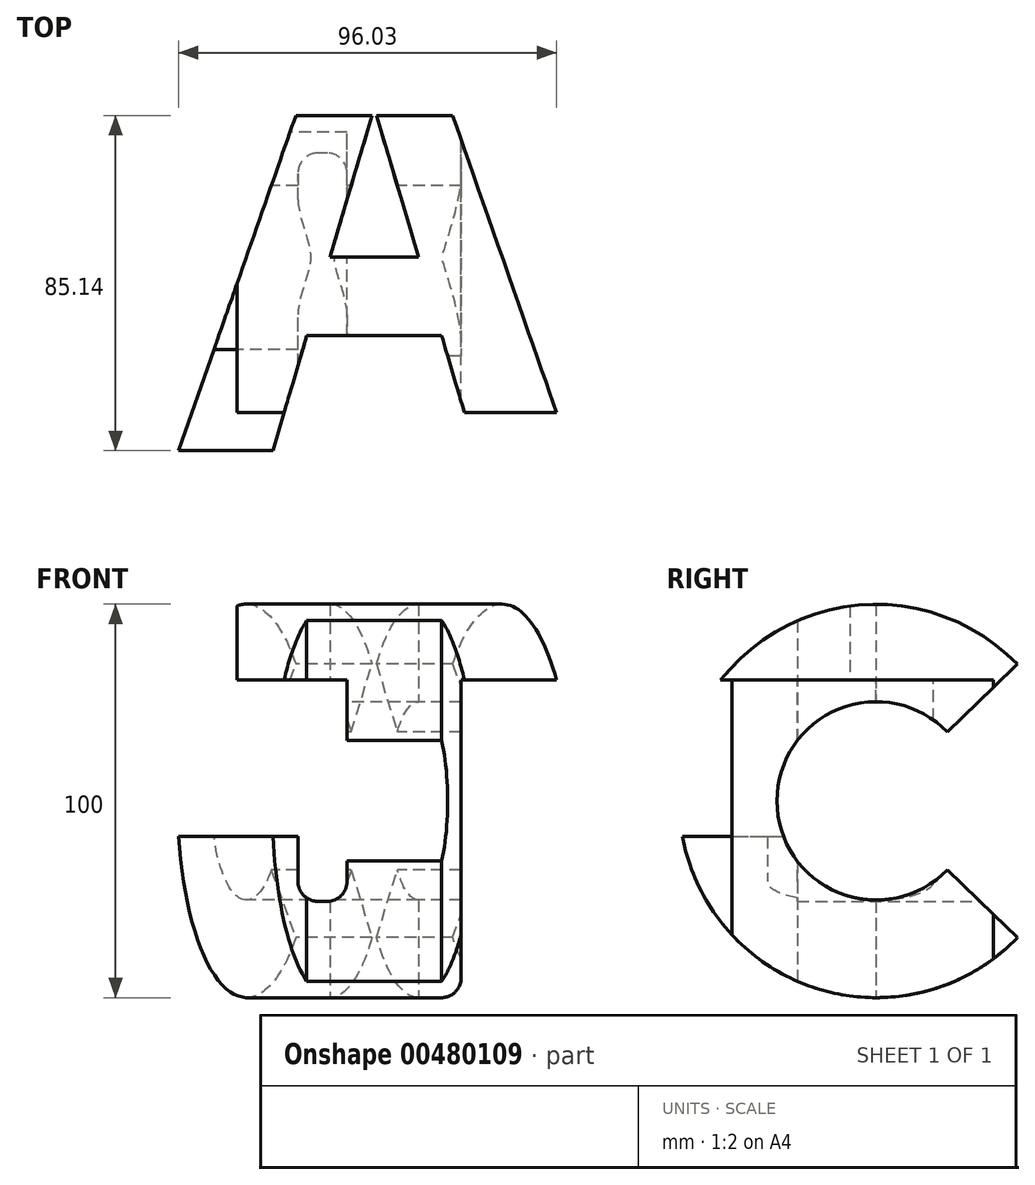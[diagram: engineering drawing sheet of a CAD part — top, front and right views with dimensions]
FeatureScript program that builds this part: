
annotation { "Feature Type Name" : "Feature", "Feature Type Description" : "" }
export const myFeature = defineFeature(function(context is Context, id is Id, definition is map)
    precondition{}
    {
        {
            var Q0;
            Q0=qCreatedBy(makeId("Top.planeOp"),FACE);
            var sketch = newSketch(context, id + "F0", { "sketchPlane" : qUnion([Q0])});
            skLineSegment(sketch, "E0.bottom", {"start": v(50, 50) * mm, "end": v(-50, 50) * mm, "construction": true});
            skLineSegment(sketch, "E0.top", {"start": v(50, -50) * mm, "end": v(-50, -50) * mm, "construction": true});
            skLineSegment(sketch, "E0.left", {"start": v(50, 50) * mm, "end": v(50, -50) * mm, "construction": true});
            skLineSegment(sketch, "E0.right", {"start": v(-50, 50) * mm, "end": v(-50, -50) * mm, "construction": true});
            skPoint(sketch, "E0.middle", {"position": v(0, 0) * mm});
            skLineSegment(sketch, "E1", {"start": v(0, 50) * mm, "end": v(15, 50) * mm});
            skLineSegment(sketch, "E2", {"start": v(0, 50) * mm, "end": v(-15, 50) * mm});
            skLineSegment(sketch, "E3", {"start": v(-50, -50) * mm, "end": v(-15, 50) * mm});
            skLineSegment(sketch, "E4", {"start": v(15, 50) * mm, "end": v(50, -50) * mm});
            skLineSegment(sketch, "E5", {"start": v(-26.01, -50) * mm, "end": v(-17.14, -20) * mm});
            skLineSegment(sketch, "E6", {"start": v(0, 37.9) * mm, "end": v(11.22, 0) * mm});
            skLineSegment(sketch, "E7", {"start": v(-50, -50) * mm, "end": v(-26.01, -50) * mm});
            skLineSegment(sketch, "E8", {"start": v(26.01, -50) * mm, "end": v(50, -50) * mm});
            skLineSegment(sketch, "E9", {"start": v(-11.22, 0) * mm, "end": v(11.22, 0) * mm});
            skLineSegment(sketch, "E10", {"start": v(-17.14, -20) * mm, "end": v(17.14, -20) * mm});
            skLineSegment(sketch, "E11.trimOffspring", {"start": v(-11.22, 0) * mm, "end": v(0, 37.9) * mm});
            skLineSegment(sketch, "E12.trimOffspring", {"start": v(17.14, -20) * mm, "end": v(26.01, -50) * mm});
            skSolve(sketch);
        }
        {
            var Q0;
            Q0=qCreatedBy(makeId("Front.planeOp"),FACE);
            var sketch = newSketch(context, id + "F1", { "sketchPlane" : qUnion([Q0])});
            skLineSegment(sketch, "E13.bottom", {"start": v(50, 50) * mm, "end": v(-50, 50) * mm, "construction": true});
            skLineSegment(sketch, "E13.top", {"start": v(50, -50) * mm, "end": v(-50, -50) * mm, "construction": true});
            skLineSegment(sketch, "E13.left", {"start": v(50, 50) * mm, "end": v(50, -50) * mm, "construction": true});
            skLineSegment(sketch, "E13.right", {"start": v(-50, 50) * mm, "end": v(-50, -50) * mm, "construction": true});
            skPoint(sketch, "E13.middle", {"position": v(0, 0) * mm});
            skLineSegment(sketch, "E14.bottom", {"start": v(50, 50) * mm, "end": v(-34.84, 50) * mm});
            skLineSegment(sketch, "E14.top", {"start": v(50, 30.68) * mm, "end": v(22.07, 30.68) * mm});
            skLineSegment(sketch, "E14.left", {"start": v(50, 50) * mm, "end": v(50, 30.68) * mm});
            skLineSegment(sketch, "E14.right", {"start": v(-34.84, 50) * mm, "end": v(-34.84, 30.68) * mm});
            skLineSegment(sketch, "E15", {"start": v(22.07, 30.68) * mm, "end": v(22.07, -45) * mm});
            skLineSegment(sketch, "E16", {"start": v(17.07, -50) * mm, "end": v(-45, -50) * mm});
            skLineSegment(sketch, "E17", {"start": v(-50, -45) * mm, "end": v(-50, -9.07) * mm});
            skLineSegment(sketch, "E18", {"start": v(-50, -9.07) * mm, "end": v(-19.37, -9.07) * mm});
            skLineSegment(sketch, "E19", {"start": v(-19.37, -9.07) * mm, "end": v(-19.37, -20.52) * mm});
            skLineSegment(sketch, "E20", {"start": v(-14.37, -25.52) * mm, "end": v(-11.9, -25.52) * mm});
            skLineSegment(sketch, "E21", {"start": v(-6.9, -20.52) * mm, "end": v(-6.9, 30.68) * mm});
            skPoint(sketch, "E22.visualSharp", {"position": v(22.07, -50) * mm});
            skArc(sketch, "E22.filletArc", {"start": v(17.07, -50) * mm, "mid": v(20.6, -48.54) * mm, "end": v(22.07, -45) * mm});
            skPoint(sketch, "E23.visualSharp", {"position": v(-50, -50) * mm});
            skArc(sketch, "E23.filletArc", {"start": v(-50, -45) * mm, "mid": v(-48.54, -48.54) * mm, "end": v(-45, -50) * mm});
            skPoint(sketch, "E24.visualSharp", {"position": v(-19.37, -25.52) * mm});
            skArc(sketch, "E24.filletArc", {"start": v(-19.37, -20.52) * mm, "mid": v(-17.9, -24.06) * mm, "end": v(-14.37, -25.52) * mm});
            skPoint(sketch, "E25.visualSharp", {"position": v(-6.9, -25.52) * mm});
            skArc(sketch, "E25.filletArc", {"start": v(-11.9, -25.52) * mm, "mid": v(-8.37, -24.06) * mm, "end": v(-6.9, -20.52) * mm});
            skLineSegment(sketch, "E26.trimOffspring", {"start": v(-6.9, 30.68) * mm, "end": v(-34.84, 30.68) * mm});
            skSolve(sketch);
        }
        {
            var Q0;
            Q0=qCreatedBy(makeId("Right.planeOp"),FACE);
            var sketch = newSketch(context, id + "F2", { "sketchPlane" : qUnion([Q0])});
            skLineSegment(sketch, "E27.bottom", {"start": v(50, 50) * mm, "end": v(-50, 50) * mm, "construction": true});
            skLineSegment(sketch, "E27.top", {"start": v(50, -50) * mm, "end": v(-50, -50) * mm, "construction": true});
            skLineSegment(sketch, "E27.left", {"start": v(50, 50) * mm, "end": v(50, -50) * mm, "construction": true});
            skLineSegment(sketch, "E27.right", {"start": v(-50, 50) * mm, "end": v(-50, -50) * mm, "construction": true});
            skPoint(sketch, "E27.middle", {"position": v(0, 0) * mm});
            skArc(sketch, "E28", {"start": v(35.97, 34.73) * mm, "mid": v(-50, 0) * mm, "end": v(35.97, -34.73) * mm});
            skArc(sketch, "E29", {"start": v(18.12, -17.5) * mm, "mid": v(-25.19, 0) * mm, "end": v(18.12, 17.5) * mm});
            skLineSegment(sketch, "E30", {"start": v(18.12, 17.5) * mm, "end": v(35.97, 34.73) * mm});
            skLineSegment(sketch, "E31", {"start": v(18.12, -17.5) * mm, "end": v(35.97, -34.73) * mm});
            skSolve(sketch);
        }
        {
            var Q0;
            Q0 = qSketchRegion(id + "F0", true);
            extrude(context, id + "F3", {"entities" : qUnion([Q0]), "endBound" : BoundingType.SYMMETRIC, "depth" : 100 * mm});
        }
        {
            var Q0;
            Q0 = qSketchRegion(id + "F1", true);
            extrude(context, id + "F4", {"entities" : qUnion([Q0]), "operationType" : NewBodyOperationType.INTERSECT, "endBound" : BoundingType.SYMMETRIC, "depth" : 100 * mm});
        }
        {
            var Q0;
            Q0 = qSketchRegion(id + "F2", true);
            extrude(context, id + "F5", {"entities" : qUnion([Q0]), "operationType" : NewBodyOperationType.INTERSECT, "endBound" : BoundingType.SYMMETRIC, "depth" : 100 * mm});
        }
    });
